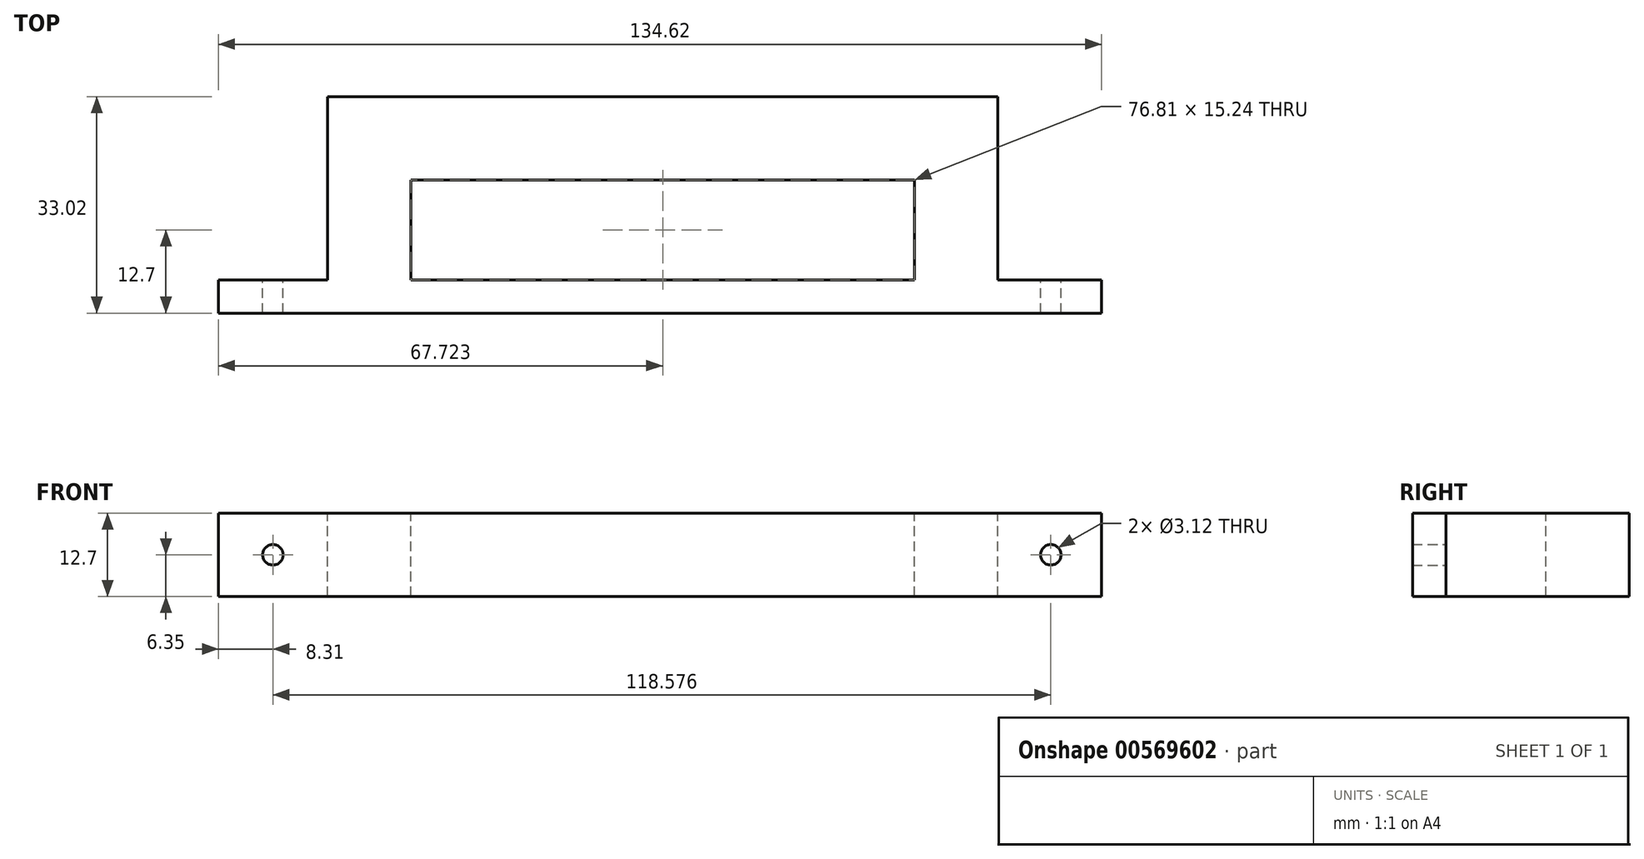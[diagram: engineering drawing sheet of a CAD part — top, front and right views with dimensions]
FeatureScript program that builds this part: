
annotation { "Feature Type Name" : "Feature", "Feature Type Description" : "" }
export const myFeature = defineFeature(function(context is Context, id is Id, definition is map)
    precondition{}
    {
        {
            var Q0;
            Q0=qCreatedBy(makeId("Front.planeOp"),FACE);
            var sketch = newSketch(context, id + "F0", { "sketchPlane" : qUnion([Q0])});
            skLineSegment(sketch, "E0.bottom", {"start": v(67.31, -6.35) * mm, "end": v(-67.31, -6.35) * mm});
            skLineSegment(sketch, "E0.top", {"start": v(67.31, 6.35) * mm, "end": v(-67.31, 6.35) * mm});
            skLineSegment(sketch, "E0.left", {"start": v(67.31, -6.35) * mm, "end": v(67.31, 6.35) * mm});
            skLineSegment(sketch, "E0.right", {"start": v(-67.31, -6.35) * mm, "end": v(-67.31, 6.35) * mm});
            skPoint(sketch, "E0.middle", {"position": v(0, 0) * mm});
            skSolve(sketch);
        }
        {
            var Q0;
            Q0 = qSketchRegion(id + "F0", true);
            extrude(context, id + "F1", {"entities" : qUnion([Q0]), "depth" : 5.08 * mm, "offsetDistance" : 25.4 * mm});
        }
        {
            var Q0;
            Q0=makeQuery(id+"F1.opExtrude","CAP_FACE",FACE,{"disambiguationData":[OSD([sQuery(id+"F0.wireOp",EDGE,"E0.bottom"),sQuery(id+"F0.wireOp",EDGE,"E0.top"),sQuery(id+"F0.wireOp",EDGE,"E0.left"),sQuery(id+"F0.wireOp",EDGE,"E0.right")])],"isStart":true});
            var sketch = newSketch(context, id + "F2", { "sketchPlane" : qUnion([Q0])});
            skLineSegment(sketch, "E1.bottom", {"start": v(-51.52, -6.35) * mm, "end": v(-38.82, -6.35) * mm});
            skLineSegment(sketch, "E1.top", {"start": v(-51.52, 6.35) * mm, "end": v(-38.82, 6.35) * mm});
            skLineSegment(sketch, "E1.left", {"start": v(-51.52, -6.35) * mm, "end": v(-51.52, 6.35) * mm});
            skLineSegment(sketch, "E1.right", {"start": v(-38.82, -6.35) * mm, "end": v(-38.82, 6.35) * mm});
            skLineSegment(sketch, "E2.bottom", {"start": v(50.7, -6.35) * mm, "end": v(38, -6.35) * mm});
            skLineSegment(sketch, "E2.top", {"start": v(50.7, 6.35) * mm, "end": v(38, 6.35) * mm});
            skLineSegment(sketch, "E2.left", {"start": v(50.7, -6.35) * mm, "end": v(50.7, 6.35) * mm});
            skLineSegment(sketch, "E2.right", {"start": v(38, -6.35) * mm, "end": v(38, 6.35) * mm});
            skSolve(sketch);
        }
        {
            var Q0;
            Q0 = qSketchRegion(id + "F2", true);
            extrude(context, id + "F3", {"entities" : qUnion([Q0]), "operationType" : NewBodyOperationType.ADD, "depth" : 27.94 * mm, "offsetDistance" : 25.4 * mm});
        }
        {
            var Q0;
            Q0=makeQuery(id+"F3.opExtrude","SWEPT_FACE",FACE,{"disambiguationData":[OSD([sQuery(id+"F2.wireOp",EDGE,"E2.left")])]});
            var sketch = newSketch(context, id + "F4", { "sketchPlane" : qUnion([Q0])});
            skLineSegment(sketch, "E3.bottom", {"start": v(-27.94, 6.35) * mm, "end": v(-15.24, 6.35) * mm});
            skLineSegment(sketch, "E3.top", {"start": v(-27.94, -6.35) * mm, "end": v(-15.24, -6.35) * mm});
            skLineSegment(sketch, "E3.left", {"start": v(-27.94, 6.35) * mm, "end": v(-27.94, -6.35) * mm});
            skLineSegment(sketch, "E3.right", {"start": v(-15.24, 6.35) * mm, "end": v(-15.24, -6.35) * mm});
            skSolve(sketch);
        }
        {
            var Q0;
            Q0 = qSketchRegion(id + "F4", true);
            extrude(context, id + "F5", {"entities" : qUnion([Q0]), "operationType" : NewBodyOperationType.ADD, "oppositeDirection" : true, "depth" : 99.31 * mm, "offsetDistance" : 25.4 * mm});
        }
        {
            var Q0;
            {var subQ0=sQuery(id+"F0.wireOp",EDGE,"E0.left");var subQ1=sQuery(id+"F0.wireOp",EDGE,"E0.top");var subQ2=sQuery(id+"F0.wireOp",EDGE,"E0.bottom");Q0=makeQuery(id+"F3.boolean.opBoolean","SPLIT",FACE,{"disambiguationData":[TD([makeQuery(id+"F1.opExtrude","SWEPT_FACE",FACE,{"disambiguationData":[OSD([subQ0])]})])],"derivedFrom":makeQuery(id+"F1.opExtrude","CAP_FACE",FACE,{"disambiguationData":[OSD([subQ2,subQ1,subQ0,sQuery(id+"F0.wireOp",EDGE,"E0.right")])],"isStart":true})});}
            var sketch = newSketch(context, id + "F6", { "sketchPlane" : qUnion([Q0])});
            skCircle(sketch, "E4", {"center": v(-59.58, 0) * mm, "radius": 1.56 * mm});
            skSolve(sketch);
        }
        {
            var Q0;
            Q0 = qSketchRegion(id + "F6", true);
            extrude(context, id + "F7", {"entities" : qUnion([Q0]), "operationType" : NewBodyOperationType.REMOVE, "oppositeDirection" : true, "depth" : 25.4 * mm, "offsetDistance" : 25.4 * mm});
        }
        {
            var Q0;
            {var subQ0=sQuery(id+"F0.wireOp",EDGE,"E0.top");var subQ1=sQuery(id+"F0.wireOp",EDGE,"E0.right");var subQ2=sQuery(id+"F0.wireOp",EDGE,"E0.bottom");Q0=makeQuery(id+"F3.boolean.opBoolean","SPLIT",FACE,{"disambiguationData":[TD([makeQuery(id+"F1.opExtrude","SWEPT_FACE",FACE,{"disambiguationData":[OSD([subQ1])]})])],"derivedFrom":makeQuery(id+"F1.opExtrude","CAP_FACE",FACE,{"disambiguationData":[OSD([subQ2,subQ0,sQuery(id+"F0.wireOp",EDGE,"E0.left"),subQ1])],"isStart":true})});}
            var sketch = newSketch(context, id + "F8", { "sketchPlane" : qUnion([Q0])});
            skCircle(sketch, "E5", {"center": v(59, 0) * mm, "radius": 1.56 * mm});
            skSolve(sketch);
        }
        {
            var Q0;
            Q0 = qSketchRegion(id + "F8", true);
            extrude(context, id + "F9", {"entities" : qUnion([Q0]), "operationType" : NewBodyOperationType.REMOVE, "oppositeDirection" : true, "depth" : 25.4 * mm, "offsetDistance" : 25.4 * mm});
        }
    });
